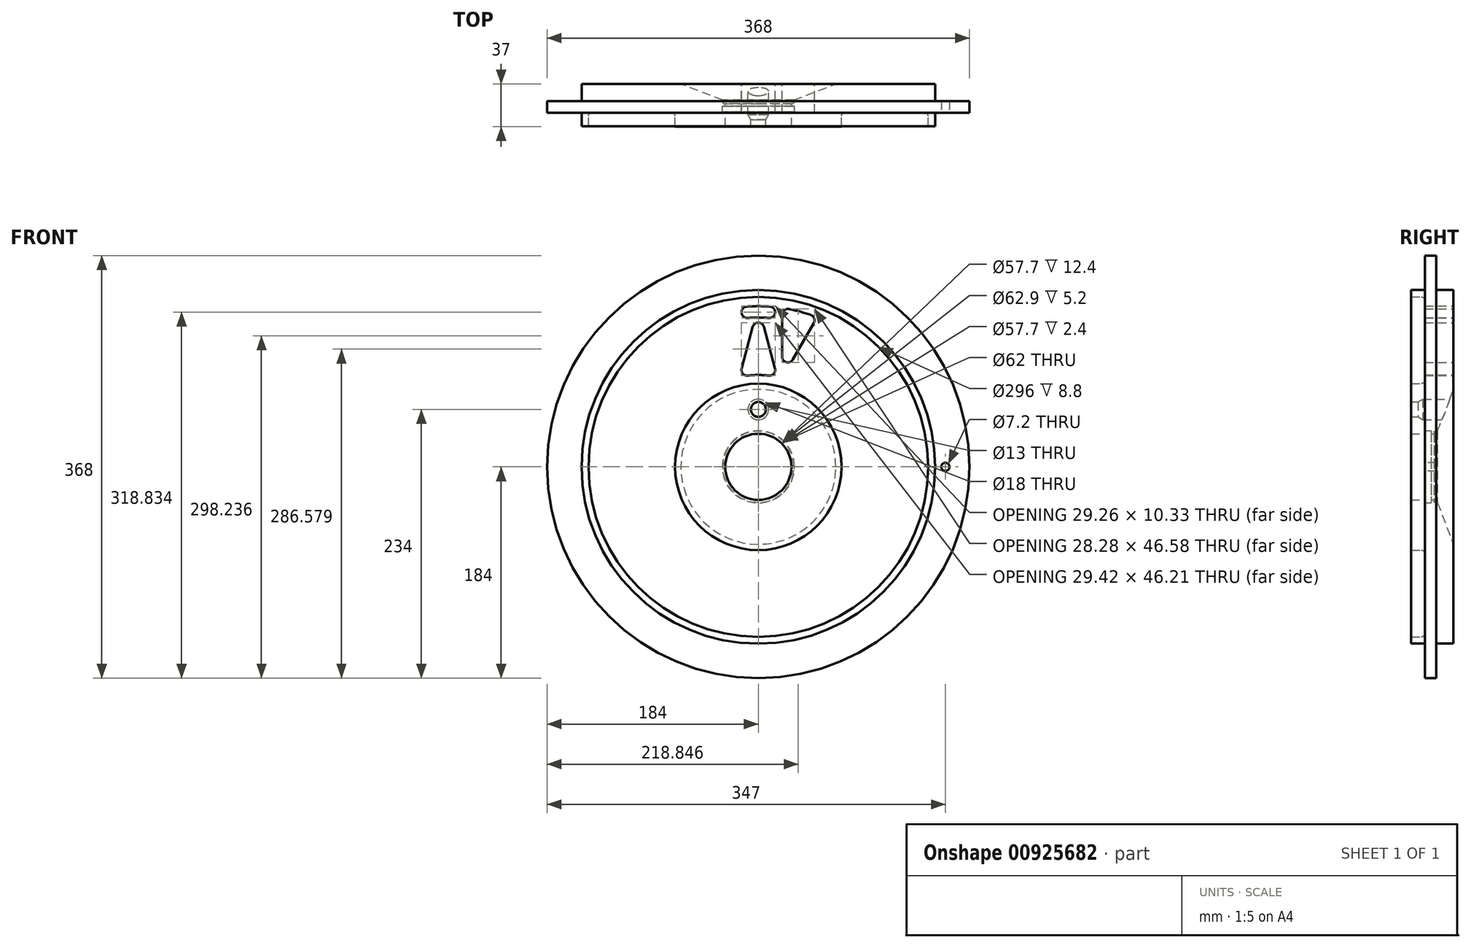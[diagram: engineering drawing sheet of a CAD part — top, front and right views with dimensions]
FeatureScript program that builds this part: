
annotation { "Feature Type Name" : "Feature", "Feature Type Description" : "" }
export const myFeature = defineFeature(function(context is Context, id is Id, definition is map)
    precondition{}
    {
        {
            var Q0;
            Q0=qCreatedBy(makeId("Top.planeOp"),FACE);
            var sketch = newSketch(context, id + "F0", { "sketchPlane" : qUnion([Q0])});
            skLineSegment(sketch, "E0", {"start": v(-72.5, 9) * mm, "end": v(-72.5, 0) * mm});
            skLineSegment(sketch, "E1", {"start": v(-72.5, 0) * mm, "end": v(-28.85, 0) * mm});
            skLineSegment(sketch, "E2", {"start": v(0, 47.35) * mm, "end": v(0, -31.33) * mm, "construction": true});
            skPoint(sketch, "E3.visualSharp", {"position": v(-72.5, 10) * mm});
            skLineSegment(sketch, "E4", {"start": v(-22.07, -0.9) * mm, "end": v(27.18, -0.9) * mm, "construction": true});
            skLineSegment(sketch, "E5", {"start": v(-154, 12) * mm, "end": v(-154, 0.2) * mm});
            skLineSegment(sketch, "E6", {"start": v(-154, 0.2) * mm, "end": v(-148, 0.2) * mm});
            skLineSegment(sketch, "E7", {"start": v(-148, 0.2) * mm, "end": v(-148, 9) * mm});
            skLineSegment(sketch, "E8", {"start": v(-28.85, 20) * mm, "end": v(-30, 20) * mm});
            skPoint(sketch, "E9.visualSharp", {"position": v(-35.7, 20) * mm});
            skLineSegment(sketch, "E10", {"start": v(-28.85, 20) * mm, "end": v(-28.85, 17.6) * mm});
            skLineSegment(sketch, "E11", {"start": v(-28.85, 17.6) * mm, "end": v(-31.45, 17.6) * mm});
            skLineSegment(sketch, "E12", {"start": v(-31.45, 17.6) * mm, "end": v(-31.45, 12.4) * mm});
            skLineSegment(sketch, "E13", {"start": v(-31.45, 12.4) * mm, "end": v(-28.85, 12.4) * mm});
            skLineSegment(sketch, "E14", {"start": v(-28.85, 12.4) * mm, "end": v(-28.85, 0) * mm});
            skLineSegment(sketch, "E15", {"start": v(-154, 12) * mm, "end": v(-184, 12) * mm});
            skLineSegment(sketch, "E16", {"start": v(-154, 37) * mm, "end": v(-67.5, 37) * mm});
            skPoint(sketch, "E17.visualSharp", {"position": v(-35, 23.4) * mm});
            skLineSegment(sketch, "E18", {"start": v(-145, 12) * mm, "end": v(-75.5, 12) * mm});
            skPoint(sketch, "E19.orphan", {"position": v(-148, 11.2) * mm});
            skPoint(sketch, "E20.visualSharp", {"position": v(-148, 12) * mm});
            skArc(sketch, "E20.filletArc", {"start": v(-145, 12) * mm, "mid": v(-147.12, 11.12) * mm, "end": v(-148, 9) * mm});
            skPoint(sketch, "E21.visualSharp", {"position": v(-72.5, 12) * mm});
            skArc(sketch, "E21.filletArc", {"start": v(-72.5, 9) * mm, "mid": v(-73.38, 11.12) * mm, "end": v(-75.5, 12) * mm});
            skLineSegment(sketch, "E22", {"start": v(-184, 12) * mm, "end": v(-184, 22) * mm});
            skLineSegment(sketch, "E23", {"start": v(-184, 22) * mm, "end": v(-154, 22) * mm});
            skLineSegment(sketch, "E24", {"start": v(-154, 22) * mm, "end": v(-154, 37) * mm});
            skLineSegment(sketch, "E25", {"start": v(-31, 23) * mm, "end": v(-67.5, 37) * mm});
            skLineSegment(sketch, "E26", {"start": v(-31, 23) * mm, "end": v(-31, 21) * mm});
            skPoint(sketch, "E27.visualSharp", {"position": v(-31, 20) * mm});
            skArc(sketch, "E27.filletArc", {"start": v(-31, 21) * mm, "mid": v(-30.7, 20.3) * mm, "end": v(-30, 20) * mm});
            skSolve(sketch);
        }
        {
            var Q0;
            Q0=makeQuery(id+"F0.imprint","IMPRINT",FACE,{"disambiguationData":[TD([[makeQuery(id+"F0.imprint","IMPRINT",EDGE,{"derivedFrom":sQuery(id+"F0.wireOp",EDGE,"E0")}),1.0]])]});
            var Q1;
            Q1=sQuery(id+"F0.wireOp",EDGE,"E2");
            revolve(context, id + "F1", {"surfaceOperationType" : NewSurfaceOperationType.NEW, "entities" : qUnion([Q0]), "axis" : qUnion([Q1]), "revolveType" : RevolveType.FULL});
        }
        {
            var Q0;
            Q0=qCreatedBy(makeId("Front.planeOp"),FACE);
            var sketch = newSketch(context, id + "F2", { "sketchPlane" : qUnion([Q0])});
            skCircle(sketch, "E28", {"center": v(163, 0) * mm, "radius": 3.6 * mm});
            skSolve(sketch);
        }
        {
            var Q0;
            Q0=qSketchRegion(id+"F2",true);
            extrude(context, id + "F3", {"entities" : qUnion([Q0]), "operationType" : NewBodyOperationType.REMOVE, "oppositeDirection" : true, "depth" : 50 * mm, "offsetDistance" : 25 * mm});
        }
        {
            var Q0;
            Q0=qCreatedBy(makeId("Right.planeOp"),FACE);
            var sketch = newSketch(context, id + "F4", { "sketchPlane" : qUnion([Q0])});
            skLineSegment(sketch, "E29", {"start": v(0, 50) * mm, "end": v(51.06, 50) * mm});
            skLineSegment(sketch, "E30", {"start": v(0, 56.5) * mm, "end": v(6, 56.5) * mm});
            skLineSegment(sketch, "E31", {"start": v(6, 56.5) * mm, "end": v(10.33, 59) * mm});
            skLineSegment(sketch, "E32", {"start": v(10.33, 59) * mm, "end": v(51.06, 59) * mm});
            skLineSegment(sketch, "E33", {"start": v(51.06, 59) * mm, "end": v(51.06, 50) * mm});
            skLineSegment(sketch, "E34", {"start": v(0, 50) * mm, "end": v(0, 56.5) * mm});
            skSolve(sketch);
        }
        {
            var Q0;
            Q0=qSketchRegion(id+"F4",true);
            var Q1;
            Q1=sQuery(id+"F4.wireOp",EDGE,"E29");
            revolve(context, id + "F5", {"operationType" : NewBodyOperationType.REMOVE, "surfaceOperationType" : NewSurfaceOperationType.NEW, "entities" : qUnion([Q0]), "axis" : qUnion([Q1]), "revolveType" : RevolveType.FULL, "oppositeDirection" : true});
        }
        {
            var Q0;
            Q0=makeQuery(id+"F1.opRevolve","SWEPT_FACE",FACE,{"disambiguationData":[OSD([sQuery(id+"F0.wireOp",EDGE,"E16")])]});
            var sketch = newSketch(context, id + "F6", { "sketchPlane" : qUnion([Q0])});
            skArc(sketch, "E35", {"start": v(9.14, 79.48) * mm, "mid": v(0, 80) * mm, "end": v(-9.14, 79.48) * mm});
            skArc(sketch, "E36", {"start": v(-26.66, 137.44) * mm, "mid": v(-36.23, 135.23) * mm, "end": v(-45.63, 132.35) * mm});
            skLineSegment(sketch, "E37", {"start": v(0, 0) * mm, "end": v(0, 168.9) * mm, "construction": true});
            skLineSegment(sketch, "E38", {"start": v(0, 0) * mm, "end": v(-51.33, 191.57) * mm, "construction": true});
            skLineSegment(sketch, "E39", {"start": v(-30.04, 93.43) * mm, "end": v(-48.33, 125.13) * mm});
            skLineSegment(sketch, "E40", {"start": v(-20.7, 95.93) * mm, "end": v(-20.7, 132.53) * mm});
            skLineSegment(sketch, "E41", {"start": v(-4.83, 121.98) * mm, "end": v(-14.54, 85.74) * mm});
            skLineSegment(sketch, "E42", {"start": v(4.83, 121.98) * mm, "end": v(14.54, 85.74) * mm});
            skArc(sketch, "E43.filletArc", {"start": v(-45.63, 132.35) * mm, "mid": v(-48.69, 129.38) * mm, "end": v(-48.33, 125.13) * mm});
            skArc(sketch, "E44.filletArc", {"start": v(-20.7, 132.53) * mm, "mid": v(-22.52, 136.39) * mm, "end": v(-26.66, 137.44) * mm});
            skArc(sketch, "E45.filletArc", {"start": v(-14.54, 85.74) * mm, "mid": v(-13.5, 81.18) * mm, "end": v(-9.14, 79.48) * mm});
            skArc(sketch, "E46.filletArc", {"start": v(9.14, 79.48) * mm, "mid": v(13.5, 81.18) * mm, "end": v(14.54, 85.74) * mm});
            skArc(sketch, "E47.filletArc", {"start": v(4.83, 121.98) * mm, "mid": v(0, 125.68) * mm, "end": v(-4.83, 121.98) * mm});
            skArc(sketch, "E48.filletArc", {"start": v(-30.04, 93.43) * mm, "mid": v(-24.41, 91.1) * mm, "end": v(-20.7, 95.93) * mm});
            skArc(sketch, "E49", {"start": v(9.29, 129.67) * mm, "mid": v(0, 130) * mm, "end": v(-9.29, 129.67) * mm});
            skArc(sketch, "E50", {"start": v(10, 139.64) * mm, "mid": v(0, 140) * mm, "end": v(-10, 139.64) * mm});
            skLineSegment(sketch, "E51.trimOffspring", {"start": v(14.6, 133.96) * mm, "end": v(14.6, 133.96) * mm});
            skLineSegment(sketch, "E52.trimOffspring", {"start": v(-14.6, 133.96) * mm, "end": v(-14.6, 133.96) * mm});
            skPoint(sketch, "E53.visualSharp", {"position": v(15.32, 139.16) * mm});
            skArc(sketch, "E53.filletArc", {"start": v(14.6, 133.96) * mm, "mid": v(13.53, 137.8) * mm, "end": v(10, 139.64) * mm});
            skArc(sketch, "E54.filletArc", {"start": v(9.29, 129.67) * mm, "mid": v(12.79, 130.77) * mm, "end": v(14.6, 133.96) * mm});
            skArc(sketch, "E55.filletArc", {"start": v(-14.6, 133.96) * mm, "mid": v(-12.79, 130.77) * mm, "end": v(-9.29, 129.67) * mm});
            skPoint(sketch, "E56.visualSharp", {"position": v(-15.32, 139.16) * mm});
            skArc(sketch, "E56.filletArc", {"start": v(-10, 139.64) * mm, "mid": v(-13.53, 137.8) * mm, "end": v(-14.6, 133.96) * mm});
            skSolve(sketch);
        }
        {
            var Q0;
            Q0 = qSketchRegion(id + "F6", true);
            extrude(context, id + "F7", {"entities" : qUnion([Q0]), "operationType" : NewBodyOperationType.REMOVE, "endBound" : BoundingType.THROUGH_ALL, "oppositeDirection" : true, "depth" : 25 * mm, "offsetDistance" : 25 * mm});
        }
    });
